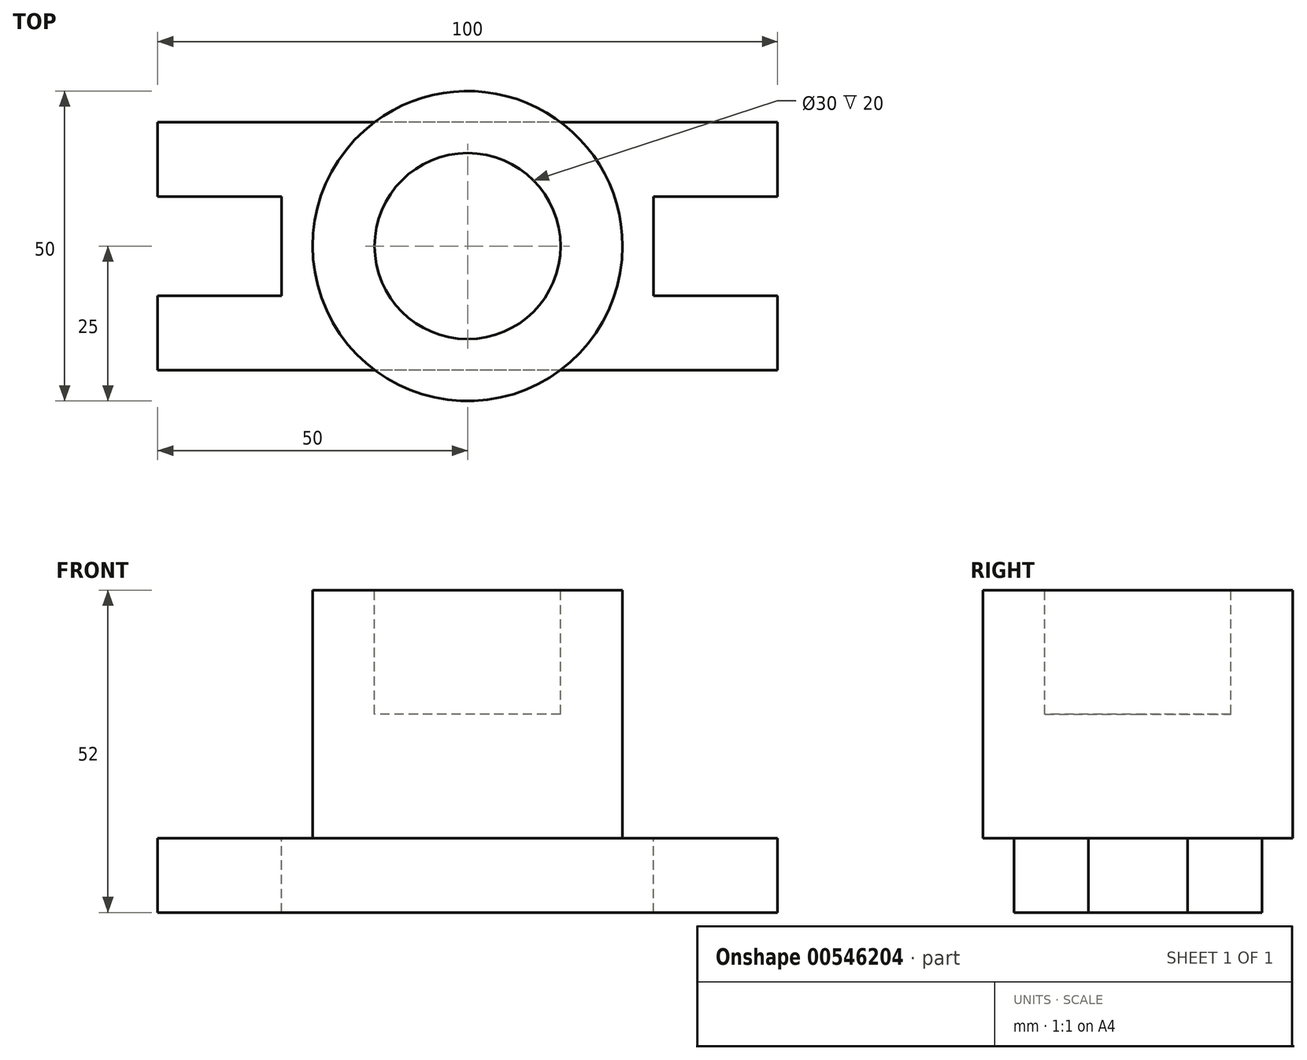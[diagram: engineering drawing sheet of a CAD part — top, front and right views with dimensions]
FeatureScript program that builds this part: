
annotation { "Feature Type Name" : "Feature", "Feature Type Description" : "" }
export const myFeature = defineFeature(function(context is Context, id is Id, definition is map)
    precondition{}
    {
        {
            var Q0;
            Q0=qCreatedBy(makeId("Top.planeOp"),FACE);
            var sketch = newSketch(context, id + "F0", { "sketchPlane" : qUnion([Q0])});
            skLineSegment(sketch, "E0.bottom", {"start": v(50, -20) * mm, "end": v(-50, -20) * mm});
            skLineSegment(sketch, "E0.top", {"start": v(50, 20) * mm, "end": v(-50, 20) * mm});
            skLineSegment(sketch, "E0.left", {"start": v(50, -20) * mm, "end": v(50, 20) * mm});
            skLineSegment(sketch, "E0.right", {"start": v(-50, -20) * mm, "end": v(-50, 20) * mm});
            skPoint(sketch, "E0.middle", {"position": v(0, 0) * mm});
            skSolve(sketch);
        }
        {
            var Q0;
            Q0 = qSketchRegion(id + "F0", true);
            extrude(context, id + "F1", {"entities" : qUnion([Q0]), "depth" : 12 * mm, "offsetDistance" : 25 * mm});
        }
        {
            var Q0;
            Q0=makeQuery(id+"F1.opExtrude","CAP_FACE",FACE,{"disambiguationData":[OSD([sQuery(id+"F0.wireOp",EDGE,"E0.bottom"),sQuery(id+"F0.wireOp",EDGE,"E0.top"),sQuery(id+"F0.wireOp",EDGE,"E0.left"),sQuery(id+"F0.wireOp",EDGE,"E0.right")])],"isStart":false});
            var sketch = newSketch(context, id + "F2", { "sketchPlane" : qUnion([Q0])});
            skLineSegment(sketch, "E1", {"start": v(-50, 20) * mm, "end": v(-50, 8) * mm, "construction": true});
            skLineSegment(sketch, "E2", {"start": v(-50, -20) * mm, "end": v(-50, -8) * mm, "construction": true});
            skLineSegment(sketch, "E3", {"start": v(0, 34.59) * mm, "end": v(0, -52.23) * mm, "construction": true});
            skLineSegment(sketch, "E4", {"start": v(-50, 8) * mm, "end": v(-30, 8) * mm});
            skLineSegment(sketch, "E5", {"start": v(-30, 8) * mm, "end": v(-30, -8) * mm});
            skLineSegment(sketch, "E6", {"start": v(-30, -8) * mm, "end": v(-50, -8) * mm});
            skLineSegment(sketch, "E7.MirrorCS", {"start": v(50, 8) * mm, "end": v(30, 8) * mm});
            skLineSegment(sketch, "E8.MirrorCS", {"start": v(30, 8) * mm, "end": v(30, -8) * mm});
            skLineSegment(sketch, "E9.MirrorCS", {"start": v(30, -8) * mm, "end": v(50, -8) * mm});
            skSolve(sketch);
        }
        {
            var Q0;
            Q0 = qSketchRegion(id + "F2", true);
            var Q1;
            {var subQ0=sQuery(id+"F2.wireOp",EDGE,"E4");Q1=makeQuery(id+"F2.imprint","IMPRINT",FACE,{"disambiguationData":[TD([[makeQuery(id+"F2.imprint","IMPRINT",EDGE,{"derivedFrom":subQ0}),-1.0]])]});}
            var Q2;
            {var subQ0=sQuery(id+"F2.wireOp",EDGE,"E7.MirrorCS");Q2=makeQuery(id+"F2.imprint","IMPRINT",FACE,{"disambiguationData":[TD([[makeQuery(id+"F2.imprint","IMPRINT",EDGE,{"derivedFrom":subQ0}),1.0]])]});}
            extrude(context, id + "F3", {"entities" : qUnion([Q0, Q1, Q2]), "operationType" : NewBodyOperationType.REMOVE, "endBound" : BoundingType.THROUGH_ALL, "oppositeDirection" : true, "depth" : 25 * mm, "offsetDistance" : 25 * mm});
        }
        {
            var Q0;
            Q0=makeQuery(id+"F1.opExtrude","CAP_FACE",FACE,{"disambiguationData":[OSD([sQuery(id+"F0.wireOp",EDGE,"E0.bottom"),sQuery(id+"F0.wireOp",EDGE,"E0.top"),sQuery(id+"F0.wireOp",EDGE,"E0.left"),sQuery(id+"F0.wireOp",EDGE,"E0.right")])],"isStart":false});
            var sketch = newSketch(context, id + "F4", { "sketchPlane" : qUnion([Q0])});
            skCircle(sketch, "E10", {"center": v(0, 0) * mm, "radius": 25 * mm});
            skSolve(sketch);
        }
        {
            var Q0;
            Q0 = qSketchRegion(id + "F4", true);
            extrude(context, id + "F5", {"entities" : qUnion([Q0]), "operationType" : NewBodyOperationType.ADD, "depth" : 40 * mm, "offsetDistance" : 25 * mm});
        }
        {
            var Q0;
            Q0=makeQuery(id+"F5.opExtrude","CAP_FACE",FACE,{"disambiguationData":[OSD([sQuery(id+"F4.wireOp",EDGE,"E10")])],"isStart":false});
            var sketch = newSketch(context, id + "F6", { "sketchPlane" : qUnion([Q0])});
            skCircle(sketch, "E11", {"center": v(0, 0) * mm, "radius": 15 * mm});
            skSolve(sketch);
        }
        {
            var Q0;
            Q0=makeQuery(id+"F6.imprint","IMPRINT",FACE,{"disambiguationData":[TD([[makeQuery(id+"F6.imprint","IMPRINT",EDGE,{"derivedFrom":sQuery(id+"F6.wireOp",EDGE,"E11")}),1.0]])]});
            extrude(context, id + "F7", {"entities" : qUnion([Q0]), "operationType" : NewBodyOperationType.REMOVE, "oppositeDirection" : true, "depth" : 20 * mm, "offsetDistance" : 25 * mm});
        }
    });
